# Revit family: Building-ElectricalVehicleCharging-GEWISS-JOINON-ION_FLOOR_MOUNTING
name_source: partatom
category: Apparecchi elettrici
units: mm (PartAtom-declared; Revit-internal decimal feet)

## family parameters
Basato su piano di lavoro = No
Condiviso = No
Mantenere orientamento annotazione = No
Numero OmniClass = 23.80.00.00
Punto di calcolo locali = Sì
Quota connettore circolare = Usa diametro
Sempre verticale = Sì
Taglio con vuoti quando caricato = No
Tipo di parte = Normale
Titolo OmniClass = Electric Power and Lighting

## types (16) — shared parameters
(Auto)restart electrical protections = No
C = a=b
Colour = Grey, Headboard RAL 7011
Corpo = Corpo
Customizations: = Yes (front)
DC Leakage check = Not needed
External treatments = Anti-corrosion and anti-graffiti
H1 = 1550 mm  [stored 5.0853 ft]
Human Interface = LED RGB and TFT Display
IDF = 88623a33-43c4-4aa8-86d3-f1eae1d19197
INPUT: = -
Immagine tipo = ION_PAVIM.jpg
Laterali = Laterali
Material = Steel sheet
Mechanical characteristics = -
Mouting and installation = Floor mounting
OUTPUT : = -
Operating temperature: = -25 +50 °C
Produttore = GEWISS S.p.A.
Protection : = Magnetothermic + Diff. Type B
Shock resistance = IK10
Testa = Testa
URL = https://www.gewiss.com
Version file RFA = 19.4
ang1 = 62.22°
h2 = 1392 mm
r2 = 79.00°
r4 = 18.00°

## per-type parameters (varying)
- GWJ1001R - COL. JOINON RFID 7,4 kW 2xT2S IP55: Charging activation=Locally managed, via RFID; Charging mode (EN 61851) :=Mode 3; Charging power=7,4 kW + 7,4 kW; Charging sockets (EN 62196)=2 x Type 2; Connectivity:=No; Current supplied (max)=32 A per socket; Descrizione=COL. JOINON RFID 7,4 kW 2xT2S IP55; External colour=Grey Chassis, Cap RAL7011; IP degree=IP55; Input current=64 Ampere; Installation type=Ground (mounting base included in the equipment); Maximum current per socket=32A + 32A; Maximum power per socket=7,4 kW + 7,4 kW; Modello=GWJ1001R; N. of sockets Type 2=2; Power max.=7,4 kW per socket; Power meter=YES (MID); Power supply (input-output)=Single-phase 35 mm²; RCCB protection=40A - 2P - Type B; RFID Reader=Yes; Rated current:=64 Ampere; Rated insulation voltage (Ui)=230 Volt; Rated voltage=230 Volt; Socket/Connector Nr. (Type)=2 (Type 2 vandal-proof socket, with shutters); Surface treatment=Anti-graffiti surface painting; Terminal blocks:=3 x 35 mm²; Thermal-magnetic protection=40A - 2P - Curve D; Total power:=15 Chilowatt; Type of residual current protection=40 A - 2P - Type B
- GWJ1001W - COL. JOINON RFID 7,4 kW 2xT2S IP55 - 3G: Charging activation=Remotely managed, via OCPP 1.6J; Charging mode (EN 61851) :=Mode 3; Charging power=7,4 kW + 7,4 kW; Charging sockets (EN 62196)=2 x Type 2; Comunication=Ethernet Kit and 4G Modem with booster antenna; Connectivity=OCPP 1.6 SOAP; Connectivity:=LAN,WIFI,4G; Current supplied (max)=32 A per socket; Descrizione=COL. JOINON RFID 7,4 kW 2xT2S IP55 - 3G; External colour=Grey Chassis, Cap RAL7011; IP degree=IP55; Input current=64 Ampere; Installation type=Ground (mounting base included in the equipment); Maximum current per socket=32A + 32A; Maximum power per socket=7,4 kW + 7,4 kW; Modello=GWJ1001W; N. of sockets Type 2=2; Power max.=7,4 kW per socket; Power meter=YES (MID); Power supply (input-output)=Single-phase 35 mm²; RCCB protection=40A - 2P - Type B; RFID Reader=Yes; Rated current:=64 Ampere; Rated insulation voltage (Ui)=230 Volt; Rated voltage=230 Volt; Socket/Connector Nr. (Type)=2 (Type 2 vandal-proof socket, with shutters); Surface treatment=Anti-graffiti surface painting; Terminal blocks:=3 x 35 mm²; Thermal-magnetic protection=40A - 2P - Curve D; Total power:=15 Chilowatt; Type of residual current protection=40 A - 2P - Type B
- GWJ1021W - COL. JOINON RFID 7,4 kW 2xT2S+SC IP55-3G: Charging activation=Remotely managed, via OCPP 1.6J; Charging power=7,4 kW + 7,4 kW; Comunication=Ethernet Kit and 4G Modem with booster antenna; Connectivity:=LAN,WIFI,4G; Current supplied (max)=32 A per socket (10 A for Type F); Descrizione=COL. JOINON RFID 7,4 kW 2xT2S+SC IP55-3G; IP degree=IP54; Modello=GWJ1021W; N. of sockets Type 2=2 (+2 domestic socket Type F); Power max.=7,4 kW per socket (2,3 kW for type F); Power meter=YES (MID); RFID Reader=Yes; Rated current:=64 Ampere; Rated insulation voltage (Ui)=230 Volt; Rated voltage=230 Volt; Socket/Connector Nr. (Type)=2 (Type 2 vandal-proof socket, with shutters) + 2(Type F); Terminal blocks:=3 x 35 mm²; Thermal-magnetic protection=40A - 2P - Curve D; Total power:=15 Chilowatt; Type of residual current protection=40 A - 2P - Type B
- GWJ1003A - COL. JOINON AUTOSTART 22 kW 2xT2S IP55: Charging activation=Free access; Charging mode (EN 61851) :=Mode 3; Charging power=22 kW + 22 kW; Charging sockets (EN 62196)=2 x Type 2; Connectivity:=No; Current supplied (max)=32 A per socket; Descrizione=COL. JOINON AUTOSTART 22 kW 2xT2S IP55; External colour=Grey Chassis, Cap RAL7011; IP degree=IP55; Input current=64 Ampere; Installation type=Ground (mounting base included in the equipment); Maximum current per socket=32A + 32A; Maximum power per socket=22 kW + 22 kW; Modello=GWJ1003A; N. of sockets Type 2=2; Power max.=22 kW per socket; Power meter=No; Power supply (input-output)=Three-phase 35mm²; RCCB protection=40A - 4P - Type B; RFID Reader=No; Rated current:=64 Ampere; Rated insulation voltage (Ui)=400 Volt; Rated voltage=400 Volt; Socket/Connector Nr. (Type)=2 (Type 2 socket, with shutters); Surface treatment=Anti-graffiti surface painting; Terminal blocks:=5 x 35 mm²; Thermal-magnetic protection=40A - 4P - D Curve; Total power:=44 Chilowatt; Type of residual current protection=40 A - 4P - Type B
- GWJ1003R - COL. JOINON RFID 22 kW 2xT2S IP55: Charging activation=Locally managed, via RFID; Charging mode (EN 61851) :=Mode 3; Charging power=22 kW + 22 kW; Charging sockets (EN 62196)=2 x Type 2; Connectivity:=No; Current supplied (max)=32 A per socket; Descrizione=COL. JOINON RFID 22 kW 2xT2S IP55; External colour=Grey Chassis, Cap RAL7011; IP degree=IP55; Input current=64 Ampere; Installation type=Ground (mounting base included in the equipment); Maximum current per socket=32A + 32A; Maximum power per socket=22 kW + 22 kW; Modello=GWJ1003R; N. of sockets Type 2=2; Power max.=22 kW per socket; Power meter=YES (MID); Power supply (input-output)=Three-phase 35mm²; RCCB protection=40A - 4P - Type B; RFID Reader=Yes; Rated current:=64 Ampere; Rated insulation voltage (Ui)=400 Volt; Rated voltage=400 Volt; Socket/Connector Nr. (Type)=2 (Type 2 vandal-proof socket, with shutters); Surface treatment=Anti-graffiti surface painting; Terminal blocks:=5 x 35 mm²; Thermal-magnetic protection=40A - 4P - D Curve; Total power:=44 Chilowatt; Type of residual current protection=40 A - 4P - Type B
- GWJ1023R - COL. JOINON RFID 22 kW 2xT2S+SC IP55: Charging activation=Locally managed, via RFID; Charging power=22 kW + 22 kW; Connectivity:=No; Current supplied (max)=32 A per socket (10 A for Type F); Descrizione=COL. JOINON RFID 22 kW 2xT2S+SC IP55; IP degree=IP54; Modello=GWJ1023R; N. of sockets Type 2=2 (+2 domestic socket Type F); Power max.=22 kW per socket (2,3 kW for type F); Power meter=YES (MID); RFID Reader=Yes; Rated current:=64 Ampere; Rated insulation voltage (Ui)=400 Volt; Rated voltage=400 Volt; Socket/Connector Nr. (Type)=2 (Type 2 vandal-proof socket, with shutters) + 2(Type F); Terminal blocks:=5 x 35 mm²; Thermal-magnetic protection=40A - 4P - D Curve; Total power:=44 Chilowatt; Type of residual current protection=40 A - 4P - Type B
- GWJ1021R - COL. JOINON RFID 7,4 kW 2xT2S+SC IP55: Charging activation=Locally managed, via RFID; Charging power=7,4 kW + 7,4 kW; Connectivity:=No; Current supplied (max)=32 A per socket (10 A for Type F); Descrizione=COL. JOINON RFID 7,4 kW 2xT2S+SC IP55; IP degree=IP54; Modello=GWJ1021R; N. of sockets Type 2=2 (+2 domestic socket Type F); Power max.=7,4 kW per socket (2,3 kW for type F); Power meter=YES (MID); RFID Reader=Yes; Rated current:=64 Ampere; Rated insulation voltage (Ui)=230 Volt; Rated voltage=230 Volt; Socket/Connector Nr. (Type)=2 (Type 2 vandal-proof socket, with shutters) + 2(Type F); Terminal blocks:=3 x 35 mm²; Thermal-magnetic protection=40A - 2P - Curve D; Total power:=15 Chilowatt; Type of residual current protection=40 A - 2P - Type B
- GWJ1001A - COL. JOINON AUTOSTART 7,4 kW 2xT2S IP55: Charging activation=Free access; Charging mode (EN 61851) :=Mode 3; Charging power=7,4 kW + 7,4 kW; Charging sockets (EN 62196)=2 x Type 2; Connectivity:=No; Current supplied (max)=32 A per socket; Descrizione=COL. JOINON AUTOSTART 7,4 kW 2xT2S IP55; External colour=Grey Chassis, Cap RAL7011; IP degree=IP55; Input current=64 Ampere; Installation type=Ground (mounting base included in the equipment); Maximum current per socket=32A + 32A; Maximum power per socket=7,4 kW + 7,4 kW; Modello=GWJ1001A; N. of sockets Type 2=2; Power max.=7,4 kW per socket; Power meter=No; Power supply (input-output)=Single-phase 35 mm²; RCCB protection=40A - 2P - Type B; RFID Reader=No; Rated current:=64 Ampere; Rated insulation voltage (Ui)=230 Volt; Rated voltage=230 Volt; Socket/Connector Nr. (Type)=2 (Type 2 socket, with shutters); Sockets Type=Type 2; Surface treatment=Anti-graffiti surface painting; Terminal blocks:=3 x 35 mm²; Thermal-magnetic protection=40A - 2P - Curve D; Total power:=15 Chilowatt; Type of residual current protection=40 A - 2P - Type B
- GWJ1002L - COL. JOINON RFID 11 kW 2xT2S IP55 - ETH: Charging activation=Remotely managed, via OCPP 1.6J; Charging mode (EN 61851) :=Mode 3; Charging power=11 kW + 11 kW; Charging sockets (EN 62196)=2 x Type 2; Comunication=Ethernet kit; Connectivity=OCPP 1.6 SOAP; Connectivity:=LAN; Current supplied (max)=16 A per socket; Descrizione=COL. JOINON RFID 11 kW 2xT2S IP55 - ETH; External colour=Grey Chassis, Cap RAL7011; IP degree=IP55; Input current=32 Ampere; Installation type=Ground (mounting base included in the equipment); Maximum current per socket=16A + 16A; Maximum power per socket=11 kW + 11 kW; Modello=GWJ1002L; N. of sockets Type 2=2; Power max.=11 kW per socket; Power meter=YES (MID); Power supply (input-output)=Three-phase 35mm²; RCCB protection=20A - 4P - Type B; RFID Reader=Yes; Rated current:=32 Ampere; Rated insulation voltage (Ui)=400 Volt; Rated voltage=400 Volt; Socket/Connector Nr. (Type)=2 (Type 2 vandal-proof socket, with shutters); Surface treatment=Anti-graffiti surface painting; Terminal blocks:=5 x 16 mm²; Thermal-magnetic protection=20A - 4P - Curve D; Total power:=22 Chilowatt; Type of residual current protection=20 A - 4P - Type B
- GWJ1001L - COL. JOINON RFID 7,4 kW 2xT2S IP55 - ETH: Charging activation=Remotely managed, via OCPP 1.6J; Charging mode (EN 61851) :=Mode 3; Charging power=7,4 kW + 7,4 kW; Charging sockets (EN 62196)=2 x Type 2; Comunication=Ethernet kit; Connectivity=OCPP 1.6 SOAP; Connectivity:=LAN; Current supplied (max)=32 A per socket; Descrizione=COL. JOINON RFID 7,4 kW 2xT2S IP55 - ETH; External colour=Grey Chassis, Cap RAL7011; IP degree=IP55; Input current=64 Ampere; Installation type=Ground (mounting base included in the equipment); Maximum current per socket=32A + 32A; Maximum power per socket=7,4 kW + 7,4 kW; Modello=GWJ1001L; N. of sockets Type 2=2; Power max.=7,4 kW per socket; Power meter=YES (MID); Power supply (input-output)=Single-phase 35 mm²; RCCB protection=40A - 2P - Type B; RFID Reader=Yes; Rated current:=64 Ampere; Rated insulation voltage (Ui)=230 Volt; Rated voltage=230 Volt; Socket/Connector Nr. (Type)=2 (Type 2 vandal-proof socket, with shutters); Surface treatment=Anti-graffiti surface painting; Terminal blocks:=3 x 35 mm²; Thermal-magnetic protection=40A - 2P - Curve D; Total power:=15 Chilowatt; Type of residual current protection=40 A - 2P - Type B
- GWJ1002W - COL. JOINON RFID 11 kW 2xT2S IP55 - 3G: Charging activation=Remotely managed, via OCPP 1.6J; Charging mode (EN 61851) :=Mode 3; Charging power=11 kW + 11 kW; Charging sockets (EN 62196)=2 x Type 2; Comunication=Ethernet Kit and 4G Modem with booster antenna; Connectivity=OCPP 1.6 SOAP; Connectivity:=LAN,WIFI,4G; Current supplied (max)=16 A per socket; Descrizione=COL. JOINON RFID 11 kW 2xT2S IP55 - 3G; External colour=Grey Chassis, Cap RAL7011; IP degree=IP55; Input current=32 Ampere; Installation type=Ground (mounting base included in the equipment); Maximum current per socket=16A + 16A; Maximum power per socket=11 kW + 11 kW; Modello=GWJ1002W; N. of sockets Type 2=2; Power max.=11 kW per socket; Power meter=YES (MID); Power supply (input-output)=Three-phase 35mm²; RCCB protection=20A - 4P - Type B; RFID Reader=Yes; Rated current:=32 Ampere; Rated insulation voltage (Ui)=400 Volt; Rated voltage=400 Volt; Socket/Connector Nr. (Type)=2 (Type 2 vandal-proof socket, with shutters); Surface treatment=Anti-graffiti surface painting; Terminal blocks:=5 x 16 mm²; Thermal-magnetic protection=20A - 4P - Curve D; Total power:=22 Chilowatt; Type of residual current protection=20 A - 4P - Type B
- GWJ1002A - COL. JOINON AUTOSTART 11 kW 2xT2S IP55: Charging activation=Free access; Charging mode (EN 61851) :=Mode 3; Charging power=11 kW + 11 kW; Charging sockets (EN 62196)=2 x Type 2; Connectivity:=No; Current supplied (max)=16 A per socket; Descrizione=COL. JOINON AUTOSTART 11 kW 2xT2S IP55; External colour=Grey Chassis, Cap RAL7011; IP degree=IP55; Input current=32 Ampere; Installation type=Ground (mounting base included in the equipment); Maximum current per socket=16A + 16A; Maximum power per socket=11 kW + 11 kW; Modello=GWJ1002A; N. of sockets Type 2=2; Power max.=11 kW per socket; Power meter=No; Power supply (input-output)=Three-phase 35mm²; RCCB protection=20A - 4P - Type B; RFID Reader=No; Rated current:=32 Ampere; Rated insulation voltage (Ui)=400 Volt; Rated voltage=400 Volt; Socket/Connector Nr. (Type)=2 (Type 2 socket, with shutters); Surface treatment=Anti-graffiti surface painting; Terminal blocks:=5 x 16 mm²; Thermal-magnetic protection=20A - 4P - Curve D; Total power:=22 Chilowatt; Type of residual current protection=20 A - 4P - Type B
- GWJ1023W - COL. JOINON RFID 22 kW 2xT2S+SC IP55-3G: Charging activation=Remotely managed, via OCPP 1.6J; Charging power=22 kW + 22 kW; Comunication=Ethernet Kit and 4G Modem with booster antenna; Connectivity:=LAN,WIFI,4G; Current supplied (max)=32 A per socket (10 A for Type F); Descrizione=COL. JOINON RFID 22 kW 2xT2S+SC IP55-3G; IP degree=IP54; Modello=GWJ1023W; N. of sockets Type 2=2 (+2 domestic socket Type F); Power max.=22 kW per socket (2,3 kW for type F); Power meter=YES (MID); RFID Reader=Yes; Rated current:=64 Ampere; Rated insulation voltage (Ui)=400 Volt; Rated voltage=400 Volt; Socket/Connector Nr. (Type)=2 (Type 2 vandal-proof socket, with shutters) + 2(Type F); Terminal blocks:=5 x 35 mm²; Thermal-magnetic protection=40A - 4P - D Curve; Total power:=44 Chilowatt; Type of residual current protection=40 A - 4P - Type B
- GWJ1002R - COL. JOINON RFID 11 kW 2xT2S IP55: Charging activation=Locally managed, via RFID; Charging mode (EN 61851) :=Mode 3; Charging power=11 kW + 11 kW; Charging sockets (EN 62196)=2 x Type 2; Connectivity:=No; Current supplied (max)=16 A per socket; Descrizione=COL. JOINON RFID 11 kW 2xT2S IP55; External colour=Grey Chassis, Cap RAL7011; IP degree=IP55; Input current=32 Ampere; Installation type=Ground (mounting base included in the equipment); Maximum current per socket=16A + 16A; Maximum power per socket=11 kW + 11 kW; Modello=GWJ1002R; N. of sockets Type 2=2; Power max.=11 kW per socket; Power meter=YES (MID); Power supply (input-output)=Three-phase 35mm²; RCCB protection=20A - 4P - Type B; RFID Reader=Yes; Rated current:=32 Ampere; Rated insulation voltage (Ui)=400 Volt; Rated voltage=400 Volt; Socket/Connector Nr. (Type)=2 (Type 2 vandal-proof socket, with shutters); Surface treatment=Anti-graffiti surface painting; Terminal blocks:=5 x 16 mm²; Thermal-magnetic protection=20A - 4P - Curve D; Total power:=22 Chilowatt; Type of residual current protection=20 A - 4P - Type B
- GWJ1003L - COL. JOINON RFID 22 kW 2xT2S IP55 - ETH: Charging activation=Remotely managed, via OCPP 1.6J; Charging mode (EN 61851) :=Mode 3; Charging power=22 kW + 22 kW; Charging sockets (EN 62196)=2 x Type 2; Comunication=Ethernet kit; Connectivity=OCPP 1.6 SOAP; Connectivity:=LAN; Current supplied (max)=32 A per socket; Descrizione=COL. JOINON RFID 22 kW 2xT2S IP55 - ETH; External colour=Grey Chassis, Cap RAL7011; IP degree=IP55; Input current=64 Ampere; Installation type=Ground (mounting base included in the equipment); Maximum current per socket=32A + 32A; Maximum power per socket=22 kW + 22 kW; Modello=GWJ1003L; N. of sockets Type 2=2; Power max.=22 kW per socket; Power meter=YES (MID); Power supply (input-output)=Three-phase 35mm²; RCCB protection=40A - 4P - Type B; RFID Reader=Yes; Rated current:=64 Ampere; Rated insulation voltage (Ui)=400 Volt; Rated voltage=400 Volt; Socket/Connector Nr. (Type)=2 (Type 2 vandal-proof socket, with shutters); Surface treatment=Anti-graffiti surface painting; Terminal blocks:=5 x 35 mm²; Thermal-magnetic protection=40A - 4P - D Curve; Total power:=44 Chilowatt; Type of residual current protection=40 A - 4P - Type B
- GWJ1003W - COL. JOINON RFID 22 kW 2xT2S IP55 - 3G: Charging activation=Remotely managed, via OCPP 1.6J; Charging mode (EN 61851) :=Mode 3; Charging power=22 kW + 22 kW; Charging sockets (EN 62196)=2 x Type 2; Comunication=Ethernet Kit and 4G Modem with booster antenna; Connectivity=OCPP 1.6 SOAP; Connectivity:=LAN,WIFI,4G; Current supplied (max)=32 A per socket; Descrizione=COL. JOINON RFID 22 kW 2xT2S IP55 - 3G; External colour=Grey Chassis, Cap RAL7011; IP degree=IP55; Input current=64 Ampere; Installation type=Ground (mounting base included in the equipment); Maximum current per socket=32A + 32A; Maximum power per socket=22 kW + 22 kW; Modello=GWJ1003W; N. of sockets Type 2=2; Power max.=22 kW per socket; Power meter=YES (MID); Power supply (input-output)=Three-phase 35mm²; RCCB protection=40A - 4P - Type B; RFID Reader=Yes; Rated current:=64 Ampere; Rated insulation voltage (Ui)=400 Volt; Rated voltage=400 Volt; Socket/Connector Nr. (Type)=2 (Type 2 vandal-proof socket, with shutters); Surface treatment=Anti-graffiti surface painting; Terminal blocks:=5 x 35 mm²; Thermal-magnetic protection=40A - 4P - D Curve; Total power:=44 Chilowatt; Type of residual current protection=40 A - 4P - Type B

note: [stored X ft] marks values corroborated as IEEE doubles in the binary element streams (Revit-internal decimal feet)
